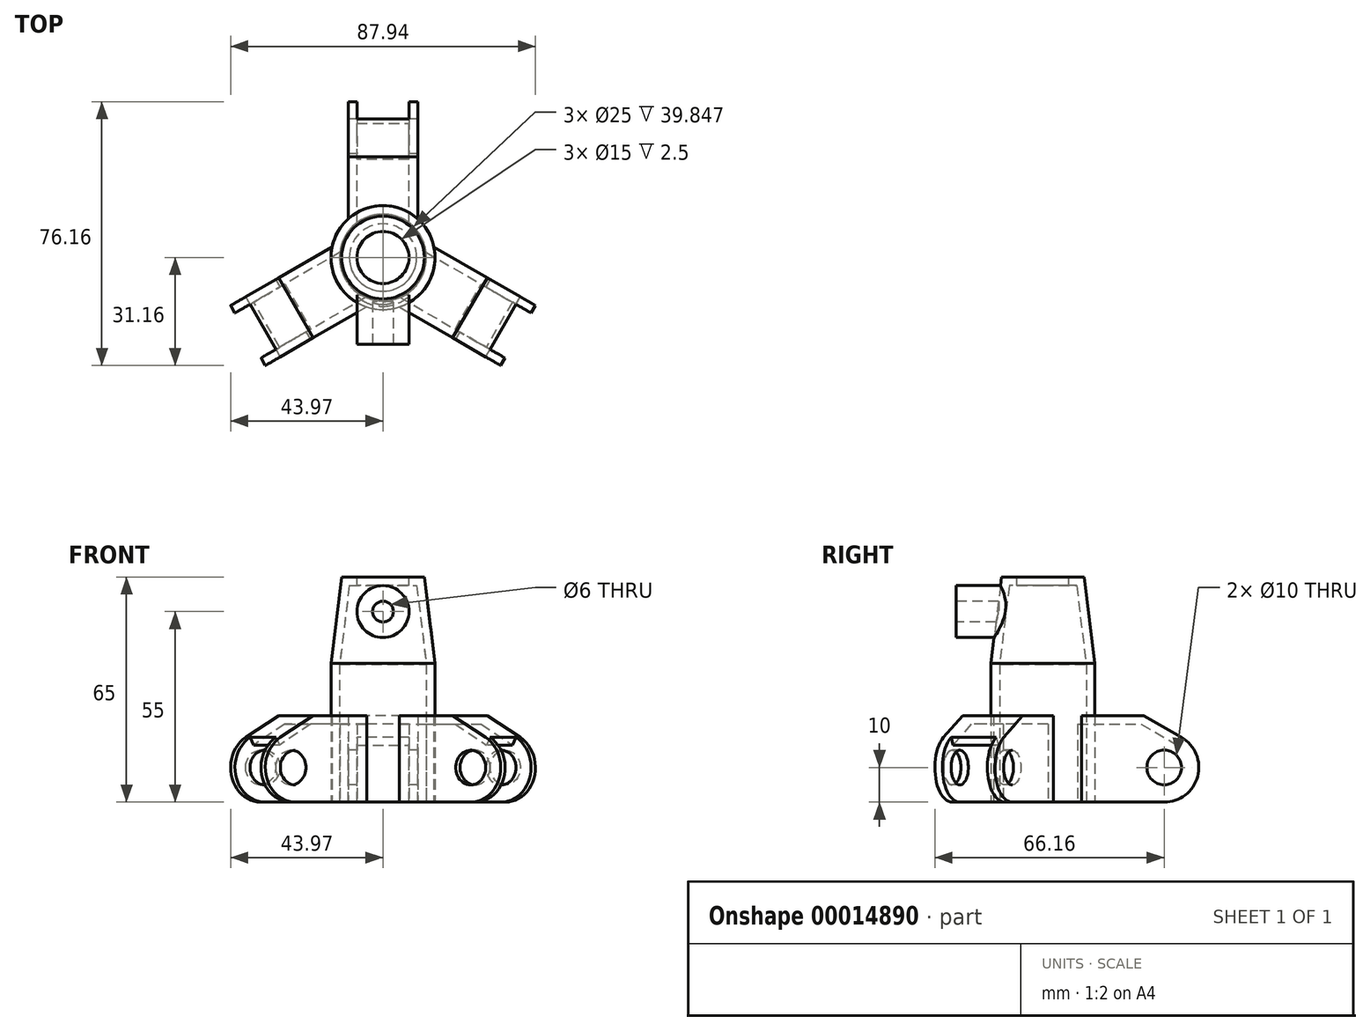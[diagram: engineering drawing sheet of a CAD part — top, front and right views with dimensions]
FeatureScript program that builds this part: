
annotation { "Feature Type Name" : "Feature", "Feature Type Description" : "" }
export const myFeature = defineFeature(function(context is Context, id is Id, definition is map)
    precondition{}
    {
        {
            var Q0;
            Q0=qCreatedBy(makeId("Top.planeOp"),FACE);
            var sketch = newSketch(context, id + "F0", { "sketchPlane" : qUnion([Q0])});
            skCircle(sketch, "E0", {"center": v(0, 0) * mm, "radius": 15 * mm});
            skSolve(sketch);
        }
        {
            var Q0;
            Q0=makeQuery(id+"F0.imprint","IMPRINT",FACE,{"disambiguationData":[TD([[makeQuery(id+"F0.imprint","IMPRINT",EDGE,{"derivedFrom":sQuery(id+"F0.wireOp",EDGE,"E0")}),1.0]])]});
            extrude(context, id + "F1", {"entities" : qUnion([Q0]), "depth" : 40 * mm});
        }
        {
            var Q0;
            Q0=makeQuery(id+"F1.opExtrude","CAP_FACE",FACE,{"disambiguationData":[OSD([sQuery(id+"F0.wireOp",EDGE,"E0")])],"isStart":false});
            var sketch = newSketch(context, id + "F2", { "sketchPlane" : qUnion([Q0])});
            skSolve(sketch);
        }
        {
            var Q0;
            Q0=makeQuery(id+"F2.imprint","IMPRINT",FACE,{"disambiguationData":[TD([[makeQuery(id+"F2.imprint","IMPRINT",EDGE,{"derivedFrom":makeQuery(id+"F1.opExtrude","CAP_EDGE",EDGE,{"disambiguationData":[OSD([sQuery(id+"F0.wireOp",EDGE,"E0")])],"isStart":false})}),1.0]])]});
            extrude(context, id + "F3", {"entities" : qUnion([Q0]), "operationType" : NewBodyOperationType.ADD, "depth" : 25 * mm, "hasDraft" : true, "draftAngle" : 7 * degree, "draftPullDirection" : true});
        }
        {
            var Q0;
            Q0=qCreatedBy(makeId("Right.planeOp"),FACE);
            var sketch = newSketch(context, id + "F4", { "sketchPlane" : qUnion([Q0])});
            skLineSegment(sketch, "E1", {"start": v(0, 0) * mm, "end": v(35, 0) * mm});
            skLineSegment(sketch, "E2", {"start": v(0, 0) * mm, "end": v(0, 25) * mm});
            skLineSegment(sketch, "E3", {"start": v(0, 25) * mm, "end": v(29.02, 25) * mm});
            skLineSegment(sketch, "E4", {"start": v(29.02, 25) * mm, "end": v(40, 18.66) * mm});
            skArc(sketch, "E5", {"start": v(40, 18.66) * mm, "mid": v(44.66, 7.41) * mm, "end": v(35, 0) * mm});
            skSolve(sketch);
        }
        {
            var Q0;
            Q0=makeQuery(id+"F4.imprint","IMPRINT",FACE,{"disambiguationData":[TD([[makeQuery(id+"F4.imprint","IMPRINT",EDGE,{"derivedFrom":sQuery(id+"F4.wireOp",EDGE,"E1")}),1.0]])]});
            extrude(context, id + "F5", {"entities" : qUnion([Q0]), "operationType" : NewBodyOperationType.ADD, "endBound" : BoundingType.SYMMETRIC, "depth" : 20 * mm});
        }
        {
            var Q0;
            Q0=makeQuery(id+"F5.opExtrude","CAP_FACE",FACE,{"disambiguationData":[OSD([sQuery(id+"F4.wireOp",EDGE,"E1"),sQuery(id+"F4.wireOp",EDGE,"E2"),sQuery(id+"F4.wireOp",EDGE,"E3"),sQuery(id+"F4.wireOp",EDGE,"E4"),sQuery(id+"F4.wireOp",EDGE,"E5")])],"isStart":true});
            var sketch = newSketch(context, id + "F6", { "sketchPlane" : qUnion([Q0])});
            skCircle(sketch, "E6", {"center": v(-35, 10) * mm, "radius": 5 * mm});
            skSolve(sketch);
        }
        {
            var Q0;
            Q0=makeQuery(id+"F6.imprint","IMPRINT",FACE,{"disambiguationData":[TD([[makeQuery(id+"F6.imprint","IMPRINT",EDGE,{"derivedFrom":sQuery(id+"F6.wireOp",EDGE,"E6")}),1.0]])]});
            extrude(context, id + "F7", {"entities" : qUnion([Q0]), "operationType" : NewBodyOperationType.REMOVE, "endBound" : BoundingType.UP_TO_NEXT, "oppositeDirection" : true, "depth" : 25 * mm});
        }
        {
            var Q0;
            Q0=makeQuery(id+"F1.opExtrude","SWEPT_BODY",BODY,{"disambiguationData":[OSD([sQuery(id+"F0.wireOp",EDGE,"E0")])]});
            var Q1;
            Q1=makeQuery(id+"F1.opExtrude","SWEPT_FACE",FACE,{"disambiguationData":[OSD([sQuery(id+"F0.wireOp",EDGE,"E0")])]});
            circularPattern(context, id + "F8", {"entities" : qUnion([Q0]), "axis" : qUnion([Q1]), "angle" : 360 * degree, "instanceCount" : 3, "equalSpace" : true});
        }
        {
            var Q0;
            Q0=makeQuery(id+"F8.opPattern","COPY",FACE,{"derivedFrom":makeQuery(id+"F5.boolean.opBoolean","MERGE",FACE,{"derivedFrom":[makeQuery(id+"F1.opExtrude","CAP_FACE",FACE,{"disambiguationData":[OSD([sQuery(id+"F0.wireOp",EDGE,"E0")])],"isStart":true}),makeQuery(id+"F5.opExtrude","SWEPT_FACE",FACE,{"disambiguationData":[OSD([sQuery(id+"F4.wireOp",EDGE,"E1")])]})]}),"instanceName":"1"});
            var Q1;
            Q1=makeQuery(id+"F5.boolean.opBoolean","MERGE",FACE,{"derivedFrom":[makeQuery(id+"F1.opExtrude","CAP_FACE",FACE,{"disambiguationData":[OSD([sQuery(id+"F0.wireOp",EDGE,"E0")])],"isStart":true}),makeQuery(id+"F5.opExtrude","SWEPT_FACE",FACE,{"disambiguationData":[OSD([sQuery(id+"F4.wireOp",EDGE,"E1")])]})]});
            var Q2;
            Q2=makeQuery(id+"F8.opPattern","COPY",FACE,{"derivedFrom":makeQuery(id+"F5.boolean.opBoolean","MERGE",FACE,{"derivedFrom":[makeQuery(id+"F1.opExtrude","CAP_FACE",FACE,{"disambiguationData":[OSD([sQuery(id+"F0.wireOp",EDGE,"E0")])],"isStart":true}),makeQuery(id+"F5.opExtrude","SWEPT_FACE",FACE,{"disambiguationData":[OSD([sQuery(id+"F4.wireOp",EDGE,"E1")])]})]}),"instanceName":"2"});
            var Q3;
            Q3=makeQuery(id+"F5.opExtrude","SWEPT_FACE",FACE,{"disambiguationData":[OSD([sQuery(id+"F4.wireOp",EDGE,"E5")])]});
            var Q4;
            Q4=makeQuery(id+"F8.opPattern","COPY",FACE,{"derivedFrom":makeQuery(id+"F5.opExtrude","SWEPT_FACE",FACE,{"disambiguationData":[OSD([sQuery(id+"F4.wireOp",EDGE,"E5")])]}),"instanceName":"2"});
            var Q5;
            Q5=makeQuery(id+"F8.opPattern","COPY",FACE,{"derivedFrom":makeQuery(id+"F5.opExtrude","SWEPT_FACE",FACE,{"disambiguationData":[OSD([sQuery(id+"F4.wireOp",EDGE,"E5")])]}),"instanceName":"1"});
            var Q6;
            Q6=makeQuery(id+"F7.boolean.opBoolean","COPY",FACE,{"derivedFrom":makeQuery(id+"F7.opExtrude","SWEPT_FACE",FACE,{"disambiguationData":[OSD([sQuery(id+"F6.wireOp",EDGE,"E6")])]})});
            var Q7;
            Q7=makeQuery(id+"F8.opPattern","COPY",FACE,{"derivedFrom":makeQuery(id+"F7.boolean.opBoolean","COPY",FACE,{"derivedFrom":makeQuery(id+"F7.opExtrude","SWEPT_FACE",FACE,{"disambiguationData":[OSD([sQuery(id+"F6.wireOp",EDGE,"E6")])]})}),"instanceName":"2"});
            var Q8;
            Q8=makeQuery(id+"F8.opPattern","COPY",FACE,{"derivedFrom":makeQuery(id+"F7.boolean.opBoolean","COPY",FACE,{"derivedFrom":makeQuery(id+"F7.opExtrude","SWEPT_FACE",FACE,{"disambiguationData":[OSD([sQuery(id+"F6.wireOp",EDGE,"E6")])]})}),"instanceName":"1"});
            shell(context, id + "F9", {"entities" : qUnion([Q0, Q1, Q2, Q3, Q4, Q5, Q6, Q7, Q8]), "thickness" : 2.5 * mm});
        }
        {
            var Q0;
            Q0=makeQuery(id+"F3.opExtrude","CAP_FACE",FACE,{"disambiguationData":[OSD([sQuery(id+"F0.wireOp",EDGE,"E0")])],"isStart":false});
            var sketch = newSketch(context, id + "F10", { "sketchPlane" : qUnion([Q0])});
            skPoint(sketch, "E7", {"position": v(0, 0) * mm});
            skSolve(sketch);
        }
        {
            var Q0;
            Q0=sQuery(id+"F10.wireOp",VERTEX,"E7");
            var Q1;
            Q1=makeQuery(id+"F1.opExtrude","SWEPT_BODY",BODY,{"disambiguationData":[OSD([sQuery(id+"F0.wireOp",EDGE,"E0")])]});
            var Q2;
            Q2=makeQuery(id+"F8.opPattern","COPY",BODY,{"derivedFrom":makeQuery(id+"F1.opExtrude","SWEPT_BODY",BODY,{"disambiguationData":[OSD([sQuery(id+"F0.wireOp",EDGE,"E0")])]}),"instanceName":"1"});
            var Q3;
            Q3=makeQuery(id+"F8.opPattern","COPY",BODY,{"derivedFrom":makeQuery(id+"F1.opExtrude","SWEPT_BODY",BODY,{"disambiguationData":[OSD([sQuery(id+"F0.wireOp",EDGE,"E0")])]}),"instanceName":"2"});
            hole(context, id + "F11", {"style" : HoleStyle.SIMPLE, "holeDiameter" : 15 * mm, "endStyle" : HoleEndStyle.THROUGH, "locations" : qUnion([Q0]), "scope" : qUnion([Q1, Q2, Q3])});
        }
        {
            var Q0;
            Q0=qCreatedBy(makeId("Front.planeOp"),FACE);
            cPlane(context, id + "F12", {"entities" : qUnion([Q0]), "cplaneType" : CPlaneType.OFFSET, "offset" : 25 * mm, "width" : 150 * mm, "height" : 150 * mm});
        }
        {
            var Q0;
            Q0=qCreatedBy(id+"F12.planeOp",FACE);
            var sketch = newSketch(context, id + "F13", { "sketchPlane" : qUnion([Q0])});
            skCircle(sketch, "E8", {"center": v(0, 55) * mm, "radius": 7.5 * mm});
            skSolve(sketch);
        }
        {
            var Q0;
            Q0=makeQuery(id+"F13.imprint","IMPRINT",FACE,{"disambiguationData":[TD([[makeQuery(id+"F13.imprint","IMPRINT",EDGE,{"derivedFrom":sQuery(id+"F13.wireOp",EDGE,"E8")}),1.0]])]});
            extrude(context, id + "F14", {"entities" : qUnion([Q0]), "endBound" : BoundingType.UP_TO_NEXT, "oppositeDirection" : true, "depth" : 25 * mm});
        }
        {
            var Q0;
            Q0=makeQuery(id+"F14.opExtrude","CAP_FACE",FACE,{"disambiguationData":[OSD([sQuery(id+"F13.wireOp",EDGE,"E8")])],"isStart":true});
            var sketch = newSketch(context, id + "F15", { "sketchPlane" : qUnion([Q0])});
            skPoint(sketch, "E9", {"position": v(0, 55) * mm});
            skSolve(sketch);
        }
        {
            var Q0;
            Q0=sQuery(id+"F15.wireOp",VERTEX,"E9");
            var Q1;
            Q1=makeQuery(id+"F14.opExtrude","SWEPT_BODY",BODY,{"disambiguationData":[OSD([sQuery(id+"F13.wireOp",EDGE,"E8")])]});
            hole(context, id + "F16", {"style" : HoleStyle.SIMPLE, "holeDiameter" : 6 * mm, "endStyle" : HoleEndStyle.BLIND, "holeDepth" : 15 * mm, "locations" : qUnion([Q0]), "scope" : qUnion([Q1])});
        }
    });
